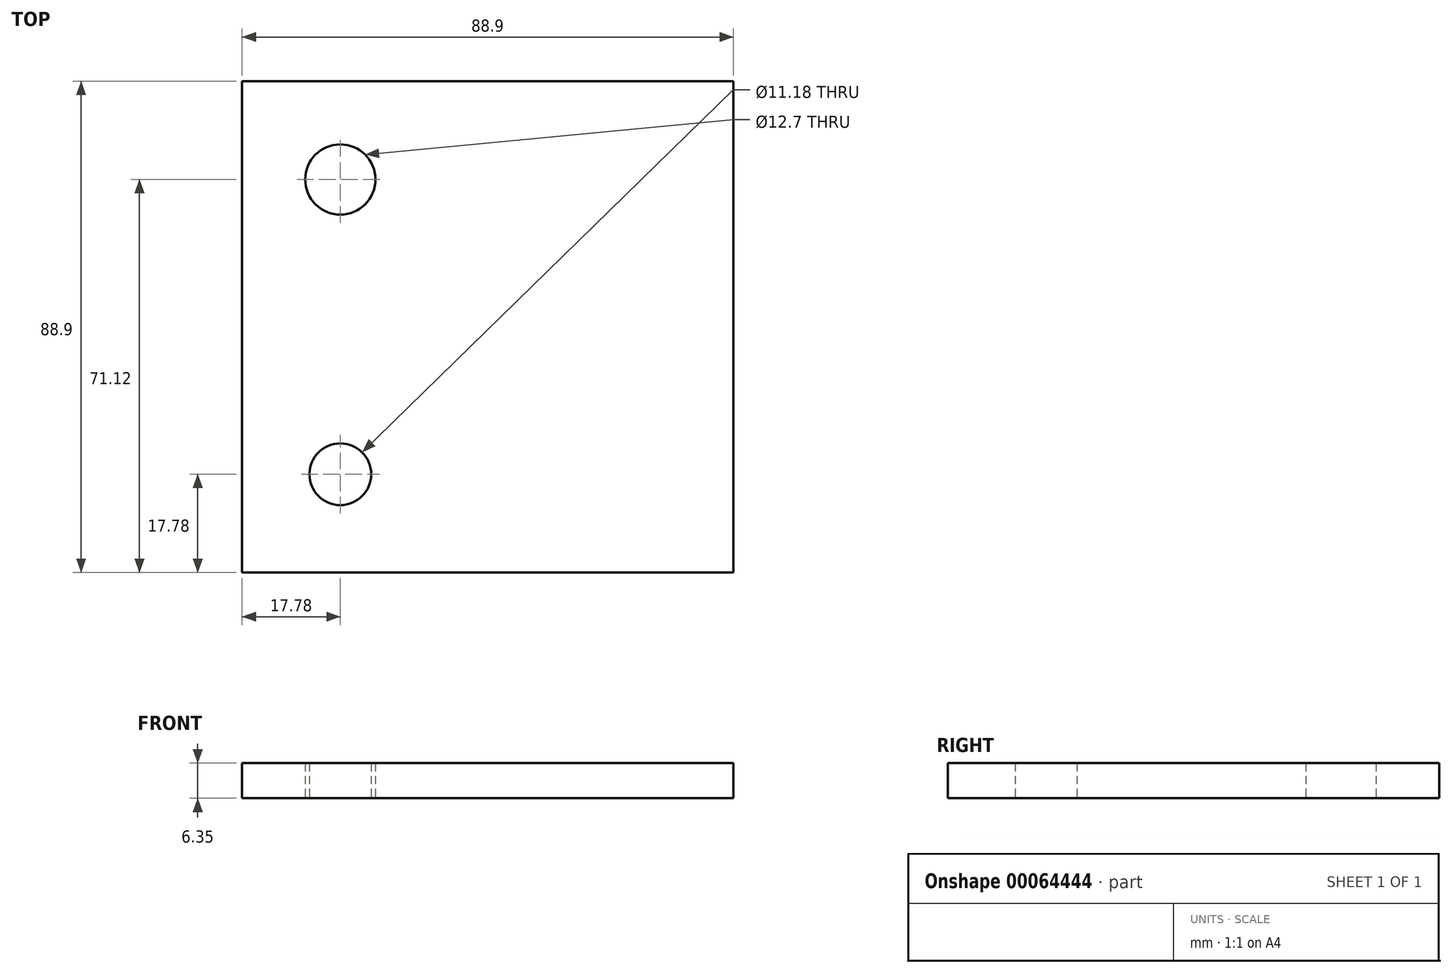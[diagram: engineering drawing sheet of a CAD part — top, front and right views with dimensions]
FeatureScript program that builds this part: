
annotation { "Feature Type Name" : "Feature", "Feature Type Description" : "" }
export const myFeature = defineFeature(function(context is Context, id is Id, definition is map)
    precondition{}
    {
        {
            var Q0;
            Q0=qCreatedBy(makeId("Top.planeOp"),FACE);
            var sketch = newSketch(context, id + "F0", { "sketchPlane" : qUnion([Q0])});
            skLineSegment(sketch, "E0.rect.bottom", {"start": v(-44.45, 44.45) * mm, "end": v(44.45, 44.45) * mm});
            skLineSegment(sketch, "E0.rect.top", {"start": v(-44.45, -44.45) * mm, "end": v(44.45, -44.45) * mm});
            skLineSegment(sketch, "E0.rect.left", {"start": v(-44.45, 44.45) * mm, "end": v(-44.45, -44.45) * mm});
            skLineSegment(sketch, "E0.rect.right", {"start": v(44.45, 44.45) * mm, "end": v(44.45, -44.45) * mm});
            skPoint(sketch, "E0.rect.middle", {"position": v(0, 0) * mm});
            skCircle(sketch, "E1", {"center": v(-26.67, -26.67) * mm, "radius": 5.59 * mm});
            skCircle(sketch, "E2", {"center": v(-26.67, 26.67) * mm, "radius": 6.35 * mm});
            skSolve(sketch);
        }
        {
            var Q0;
            Q0 = qSketchRegion(id + "F0", true);
            extrude(context, id + "F1", {"entities" : qUnion([Q0]), "depth" : 6.35 * mm});
        }
    });
